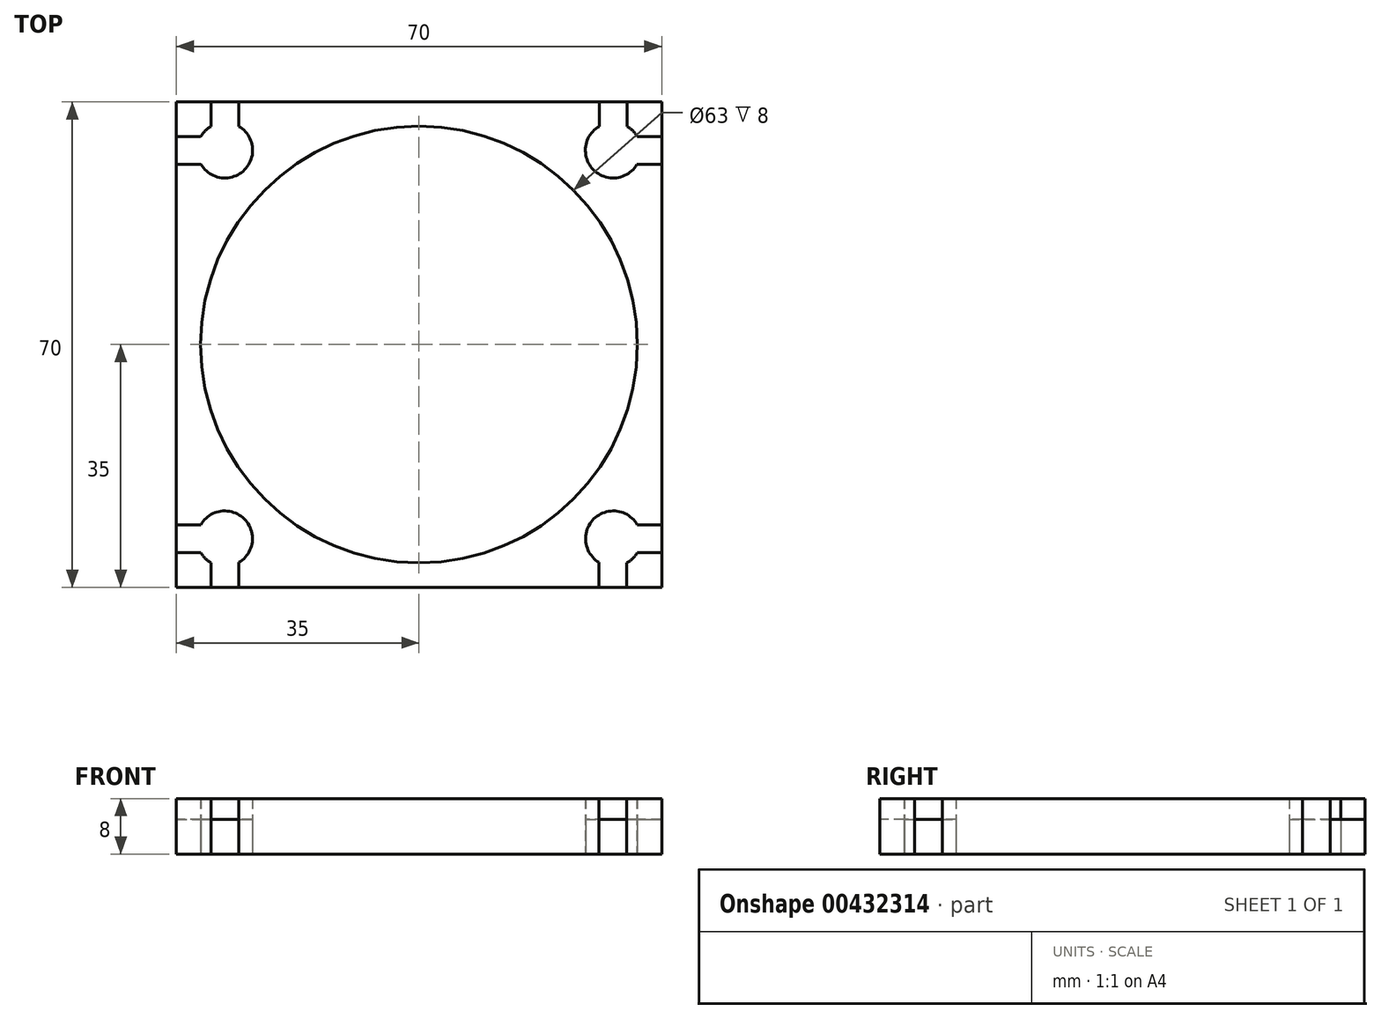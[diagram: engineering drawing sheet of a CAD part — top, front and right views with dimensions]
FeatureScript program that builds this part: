
annotation { "Feature Type Name" : "Feature", "Feature Type Description" : "" }
export const myFeature = defineFeature(function(context is Context, id is Id, definition is map)
    precondition{}
    {
        {
            var Q0;
            Q0=qCreatedBy(makeId("Top.planeOp"),FACE);
            var sketch = newSketch(context, id + "F0", { "sketchPlane" : qUnion([Q0])});
            skCircle(sketch, "E0", {"center": v(0, 0) * mm, "radius": 31.5 * mm});
            skLineSegment(sketch, "E1.bottom", {"start": v(-35, 35) * mm, "end": v(35, 35) * mm});
            skLineSegment(sketch, "E1.top", {"start": v(-35, -35) * mm, "end": v(35, -35) * mm});
            skLineSegment(sketch, "E1.left", {"start": v(-35, 35) * mm, "end": v(-35, -35) * mm});
            skLineSegment(sketch, "E1.right", {"start": v(35, 35) * mm, "end": v(35, -35) * mm});
            skLineSegment(sketch, "E2", {"start": v(-35, 35) * mm, "end": v(35, -35) * mm, "construction": true});
            skLineSegment(sketch, "E3", {"start": v(35, 35) * mm, "end": v(-35, -35) * mm, "construction": true});
            skLineSegment(sketch, "E4", {"start": v(35, -35) * mm, "end": v(35, -30) * mm});
            skLineSegment(sketch, "E5", {"start": v(35, -35) * mm, "end": v(30.51, -35) * mm});
            skLineSegment(sketch, "E6", {"start": v(35, 35) * mm, "end": v(35, 30.32) * mm, "construction": true});
            skLineSegment(sketch, "E7", {"start": v(-35, 35) * mm, "end": v(-31.99, 35) * mm});
            skLineSegment(sketch, "E8", {"start": v(-35, 35) * mm, "end": v(-28, 35) * mm});
            skLineSegment(sketch, "E9.bottom", {"start": v(-28, 28.02) * mm, "end": v(-28.02, 28.02) * mm, "construction": true});
            skLineSegment(sketch, "E9.top", {"start": v(-25.5, 41.98) * mm, "end": v(-30.5, 41.98) * mm, "construction": true});
            skPoint(sketch, "E9.middle", {"position": v(-28, 35) * mm});
            skLineSegment(sketch, "E10.trimOffspring", {"start": v(-28, 28.02) * mm, "end": v(-28, 28) * mm, "construction": true});
            skLineSegment(sketch, "E11", {"start": v(-25.5, 35) * mm, "end": v(-30.5, 35) * mm});
            skLineSegment(sketch, "E12", {"start": v(-28, 35) * mm, "end": v(-28, 28) * mm, "construction": true});
            skArc(sketch, "E13", {"start": v(-31.44, 25.98) * mm, "mid": v(-25.15, 25.21) * mm, "end": v(-26, 31.49) * mm});
            skLineSegment(sketch, "E14.0", {"start": v(-26, 35) * mm, "end": v(-26, 31.49) * mm});
            skLineSegment(sketch, "E15.0", {"start": v(-28, 27.98) * mm, "end": v(-35, 27.98) * mm, "construction": true});
            skLineSegment(sketch, "E16.0", {"start": v(-30, 35) * mm, "end": v(-30, 31.49) * mm});
            skLineSegment(sketch, "E17.0", {"start": v(-29.98, 29.98) * mm, "end": v(-30, 29.98) * mm});
            skLineSegment(sketch, "E18.trimOffspring", {"start": v(-30, 30) * mm, "end": v(-30, 29.98) * mm});
            skLineSegment(sketch, "E19.trimOffspring", {"start": v(-30, 28.02) * mm, "end": v(-30, 28) * mm});
            skLineSegment(sketch, "E20.trimOffspring", {"start": v(-31.5, 29.98) * mm, "end": v(-35, 29.98) * mm});
            skLineSegment(sketch, "E21.0", {"start": v(-31.44, 25.98) * mm, "end": v(-35, 25.98) * mm});
            skArc(sketch, "E22.trimOffspring", {"start": v(-30, 31.49) * mm, "mid": v(-30.85, 30.83) * mm, "end": v(-31.5, 29.98) * mm});
            skLineSegment(sketch, "E23", {"start": v(0, 0) * mm, "end": v(0, 35) * mm, "construction": true});
            skLineSegment(sketch, "E24.MirrorCS", {"start": v(28, 28.02) * mm, "end": v(28, 28) * mm, "construction": true});
            skLineSegment(sketch, "E25.MirrorCS", {"start": v(28, 28.02) * mm, "end": v(28.02, 28.02) * mm, "construction": true});
            skLineSegment(sketch, "E26.MirrorCS", {"start": v(29.98, 29.98) * mm, "end": v(30, 29.98) * mm});
            skLineSegment(sketch, "E27.MirrorCS", {"start": v(30, 30) * mm, "end": v(30, 29.98) * mm});
            skLineSegment(sketch, "E28.MirrorCS", {"start": v(30, 28.02) * mm, "end": v(30, 28) * mm});
            skArc(sketch, "E29.MirrorCS", {"start": v(30, 31.49) * mm, "mid": v(30.85, 30.83) * mm, "end": v(31.5, 29.98) * mm});
            skLineSegment(sketch, "E30.MirrorCS", {"start": v(30, 35) * mm, "end": v(30, 31.49) * mm});
            skLineSegment(sketch, "E31.MirrorCS", {"start": v(35, 35) * mm, "end": v(31.99, 35) * mm});
            skLineSegment(sketch, "E32.MirrorCS", {"start": v(28, 27.98) * mm, "end": v(35, 27.98) * mm, "construction": true});
            skLineSegment(sketch, "E33.MirrorCS", {"start": v(31.5, 29.98) * mm, "end": v(35, 29.98) * mm});
            skLineSegment(sketch, "E34.MirrorCS", {"start": v(28, 35) * mm, "end": v(28, 28) * mm, "construction": true});
            skPoint(sketch, "E35.MirrorP", {"position": v(28, 35) * mm});
            skLineSegment(sketch, "E36.MirrorCS", {"start": v(31.44, 25.98) * mm, "end": v(35, 25.98) * mm});
            skLineSegment(sketch, "E37.MirrorCS", {"start": v(35, 35) * mm, "end": v(28, 35) * mm});
            skArc(sketch, "E38.MirrorCS", {"start": v(31.44, 25.98) * mm, "mid": v(25.15, 25.21) * mm, "end": v(26, 31.49) * mm});
            skLineSegment(sketch, "E39.MirrorCS", {"start": v(26, 35) * mm, "end": v(26, 31.49) * mm});
            skLineSegment(sketch, "E40.MirrorCS", {"start": v(-25.98, -31.44) * mm, "end": v(-25.98, -35) * mm});
            skArc(sketch, "E41.MirrorCS", {"start": v(-25.98, -31.44) * mm, "mid": v(-25.21, -25.15) * mm, "end": v(-31.49, -26) * mm});
            skLineSegment(sketch, "E42.MirrorCS", {"start": v(-35, -26) * mm, "end": v(-31.49, -26) * mm});
            skLineSegment(sketch, "E43.MirrorCS", {"start": v(-35, -28) * mm, "end": v(-28, -28) * mm, "construction": true});
            skLineSegment(sketch, "E44.MirrorCS", {"start": v(-35, -30) * mm, "end": v(-31.49, -30) * mm});
            skLineSegment(sketch, "E45.MirrorCS", {"start": v(-29.98, -31.5) * mm, "end": v(-29.98, -35) * mm});
            skLineSegment(sketch, "E46.MirrorCS", {"start": v(28.02, -28) * mm, "end": v(28, -28) * mm, "construction": true});
            skLineSegment(sketch, "E47.MirrorCS", {"start": v(28.02, -28) * mm, "end": v(28.02, -28.02) * mm, "construction": true});
            skLineSegment(sketch, "E48.MirrorCS", {"start": v(29.98, -29.98) * mm, "end": v(29.98, -30) * mm});
            skLineSegment(sketch, "E49.MirrorCS", {"start": v(30, -30) * mm, "end": v(29.98, -30) * mm});
            skLineSegment(sketch, "E50.MirrorCS", {"start": v(28.02, -30) * mm, "end": v(28, -30) * mm});
            skLineSegment(sketch, "E51.MirrorCS", {"start": v(35, -30) * mm, "end": v(31.49, -30) * mm});
            skLineSegment(sketch, "E52.MirrorCS", {"start": v(35, -35) * mm, "end": v(35, -31.99) * mm});
            skArc(sketch, "E53.MirrorCS", {"start": v(31.49, -30) * mm, "mid": v(30.83, -30.85) * mm, "end": v(29.98, -31.5) * mm});
            skLineSegment(sketch, "E54.MirrorCS", {"start": v(35, -25.5) * mm, "end": v(35, -30.5) * mm});
            skLineSegment(sketch, "E55.MirrorCS", {"start": v(35, -35) * mm, "end": v(35, -28) * mm});
            skLineSegment(sketch, "E56.MirrorCS", {"start": v(27.98, -28) * mm, "end": v(27.98, -35) * mm, "construction": true});
            skLineSegment(sketch, "E57.MirrorCS", {"start": v(35, -35) * mm, "end": v(-35, -35) * mm});
            skLineSegment(sketch, "E58.MirrorCS", {"start": v(35, -35) * mm, "end": v(-35, 35) * mm, "construction": true});
            skLineSegment(sketch, "E59.MirrorCS", {"start": v(35, -28) * mm, "end": v(28, -28) * mm, "construction": true});
            skLineSegment(sketch, "E60.MirrorCS", {"start": v(25.98, -31.44) * mm, "end": v(25.98, -35) * mm});
            skLineSegment(sketch, "E61.MirrorCS", {"start": v(35, -35) * mm, "end": v(35, 35) * mm});
            skArc(sketch, "E62.MirrorCS", {"start": v(25.98, -31.44) * mm, "mid": v(25.21, -25.15) * mm, "end": v(31.49, -26) * mm});
            skLineSegment(sketch, "E63.MirrorCS", {"start": v(29.98, -31.5) * mm, "end": v(29.98, -35) * mm});
            skPoint(sketch, "E64.MirrorP", {"position": v(35, -28) * mm});
            skLineSegment(sketch, "E65.MirrorCS", {"start": v(35, -26) * mm, "end": v(31.49, -26) * mm});
            skArc(sketch, "E66.MirrorCS", {"start": v(-31.49, -30) * mm, "mid": v(-30.83, -30.85) * mm, "end": v(-29.98, -31.5) * mm});
            skSolve(sketch);
        }
        {
            var Q0;
            Q0=makeQuery(id+"F0.imprint","IMPRINT",FACE,{"disambiguationData":[TD([[makeQuery(id+"F0.imprint","IMPRINT",EDGE,{"derivedFrom":sQuery(id+"F0.wireOp",EDGE,"E0")}),-1.0]])]});
            var Q1;
            Q1 = qSketchRegion(id + "F2", true);
            extrude(context, id + "F1", {"entities" : qUnion([Q0, Q1]), "depth" : 8 * mm});
        }
        {
            var Q0;
            Q0=makeQuery(id+"F1.opExtrude","CAP_FACE",FACE,{"disambiguationData":[OSD([sQuery(id+"F0.wireOp",EDGE,"E0"),sQuery(id+"F0.wireOp",EDGE,"E1.bottom"),sQuery(id+"F0.wireOp",EDGE,"E1.top"),sQuery(id+"F0.wireOp",EDGE,"E1.left"),sQuery(id+"F0.wireOp",EDGE,"E1.right")])],"isStart":false});
            var sketch = newSketch(context, id + "F2", { "sketchPlane" : qUnion([Q0])});
            skCircle(sketch, "E67", {"center": v(0, 0) * mm, "radius": 33 * mm});
            skSolve(sketch);
        }
        {
            var Q0;
            {var subQ0=sQuery(id+"F0.wireOp",EDGE,"E16.0");Q0=makeQuery(id+"F0.imprint","IMPRINT",FACE,{"disambiguationData":[TD([[makeQuery(id+"F0.imprint","IMPRINT",EDGE,{"derivedFrom":subQ0}),-1.0]])]});}
            extrude(context, id + "F3", {"entities" : qUnion([Q0]), "depth" : 8 * mm});
        }
        {
            var Q0;
            Q0=makeQuery(id+"F0.imprint","IMPRINT",FACE,{"disambiguationData":[TD([[makeQuery(id+"F0.imprint","IMPRINT",EDGE,{"derivedFrom":sQuery(id+"F0.wireOp",EDGE,"E13")}),1.0]])]});
            extrude(context, id + "F4", {"entities" : qUnion([Q0]), "depth" : 5 * mm});
        }
        {
            var Q0;
            {var subQ1=sQuery(id+"F0.wireOp",EDGE,"E51.MirrorCS");Q0=makeQuery(id+"F0.imprint","IMPRINT",FACE,{"disambiguationData":[TD([[makeQuery(id+"F0.imprint","IMPRINT",EDGE,{"derivedFrom":subQ1}),1.0]])]});}
            var Q1;
            {var subQ1=sQuery(id+"F0.wireOp",EDGE,"E44.MirrorCS");Q1=makeQuery(id+"F0.imprint","IMPRINT",FACE,{"disambiguationData":[TD([[makeQuery(id+"F0.imprint","IMPRINT",EDGE,{"derivedFrom":subQ1}),-1.0]])]});}
            var Q2;
            Q2=makeQuery(id+"F0.imprint","IMPRINT",FACE,{"disambiguationData":[TD([[makeQuery(id+"F0.imprint","IMPRINT",EDGE,{"derivedFrom":sQuery(id+"F0.wireOp",EDGE,"E29.MirrorCS")}),1.0]])]});
            extrude(context, id + "F5", {"entities" : qUnion([Q0, Q1, Q2]), "depth" : 8 * mm});
        }
        {
            var Q0;
            {var subQ3=sQuery(id+"F0.wireOp",EDGE,"E51.MirrorCS");Q0=makeQuery(id+"F0.imprint","IMPRINT",FACE,{"disambiguationData":[TD([[makeQuery(id+"F0.imprint","IMPRINT",EDGE,{"derivedFrom":subQ3}),-1.0]])]});}
            var Q1;
            {var subQ3=sQuery(id+"F0.wireOp",EDGE,"E40.MirrorCS");Q1=makeQuery(id+"F0.imprint","IMPRINT",FACE,{"disambiguationData":[TD([[makeQuery(id+"F0.imprint","IMPRINT",EDGE,{"derivedFrom":subQ3}),-1.0]])]});}
            var Q2;
            Q2=makeQuery(id+"F0.imprint","IMPRINT",FACE,{"disambiguationData":[TD([[makeQuery(id+"F0.imprint","IMPRINT",EDGE,{"derivedFrom":sQuery(id+"F0.wireOp",EDGE,"E29.MirrorCS")}),-1.0]])]});
            extrude(context, id + "F6", {"entities" : qUnion([Q0, Q1, Q2]), "depth" : 5 * mm});
        }
    });
